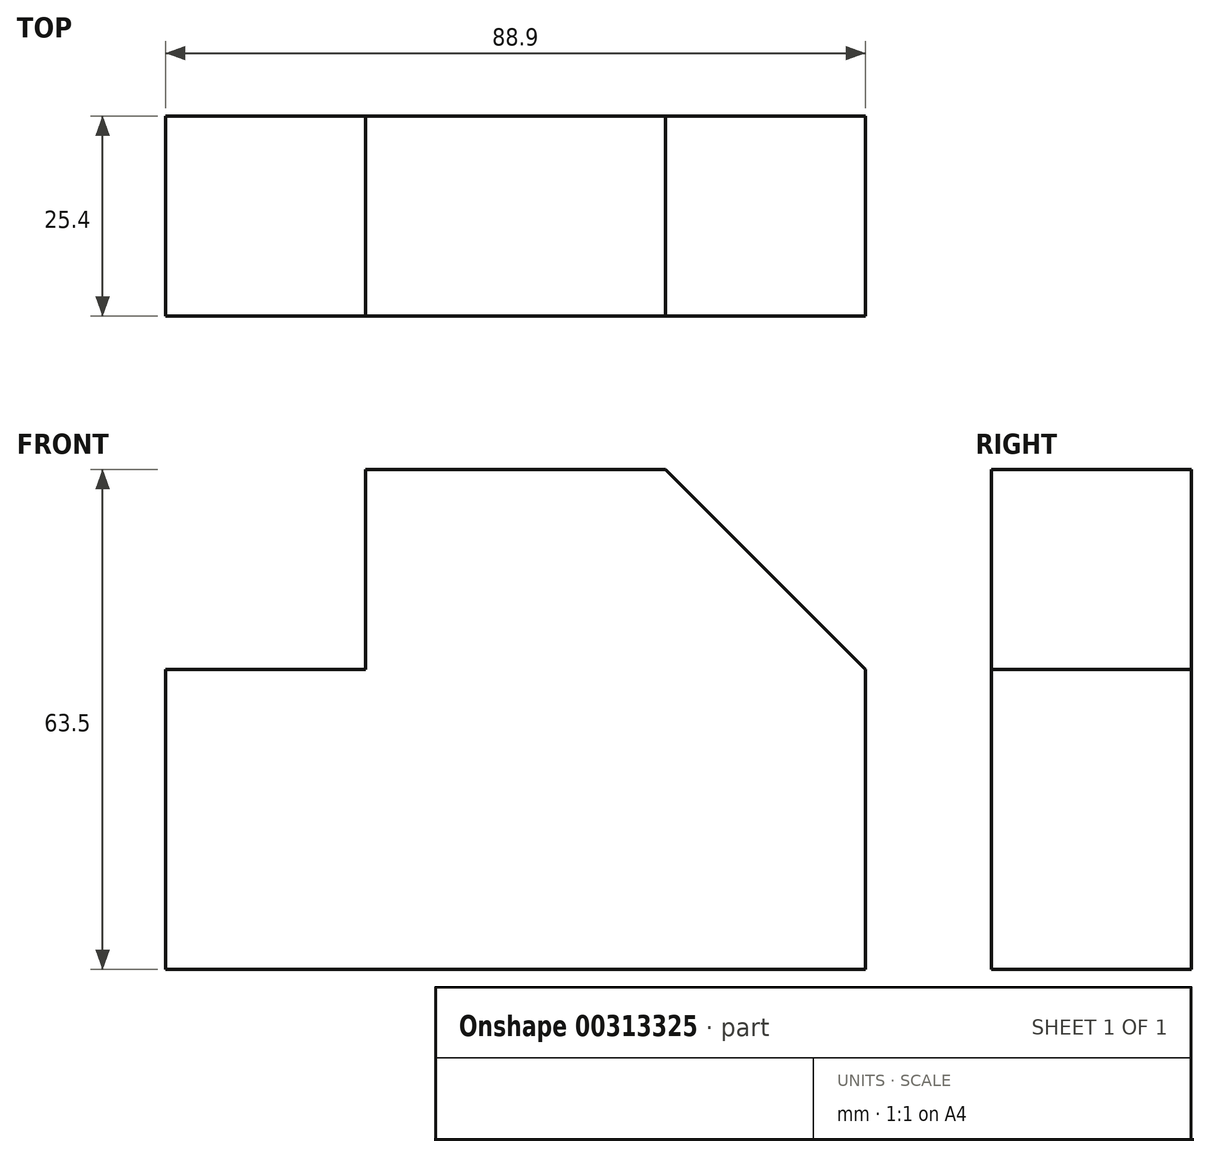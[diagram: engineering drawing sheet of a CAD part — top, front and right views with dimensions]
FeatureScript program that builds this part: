
annotation { "Feature Type Name" : "Feature", "Feature Type Description" : "" }
export const myFeature = defineFeature(function(context is Context, id is Id, definition is map)
    precondition{}
    {
        {
            var Q0;
            Q0=qCreatedBy(makeId("Front.planeOp"),FACE);
            var sketch = newSketch(context, id + "F0", { "sketchPlane" : qUnion([Q0])});
            skLineSegment(sketch, "E0", {"start": v(-66.87, 19.69) * mm, "end": v(-66.87, -18.41) * mm});
            skLineSegment(sketch, "E1", {"start": v(-66.87, 19.69) * mm, "end": v(-41.47, 19.69) * mm});
            skLineSegment(sketch, "E2", {"start": v(-41.47, 19.69) * mm, "end": v(-41.47, 45.09) * mm});
            skLineSegment(sketch, "E3", {"start": v(-41.47, 45.09) * mm, "end": v(-3.37, 45.09) * mm});
            skLineSegment(sketch, "E4", {"start": v(-66.87, -18.41) * mm, "end": v(22.03, -18.41) * mm});
            skLineSegment(sketch, "E5", {"start": v(22.03, -18.41) * mm, "end": v(22.03, 19.69) * mm});
            skLineSegment(sketch, "E6", {"start": v(-3.37, 45.09) * mm, "end": v(22.03, 19.69) * mm});
            skSolve(sketch);
        }
        {
            var Q0;
            Q0=makeQuery(id+"F0.imprint","IMPRINT",FACE,{"disambiguationData":[TD([[makeQuery(id+"F0.imprint","IMPRINT",EDGE,{"derivedFrom":sQuery(id+"F0.wireOp",EDGE,"E0")}),1.0]])]});
            extrude(context, id + "F1", {"entities" : qUnion([Q0]), "depth" : 25.4 * mm});
        }
    });
